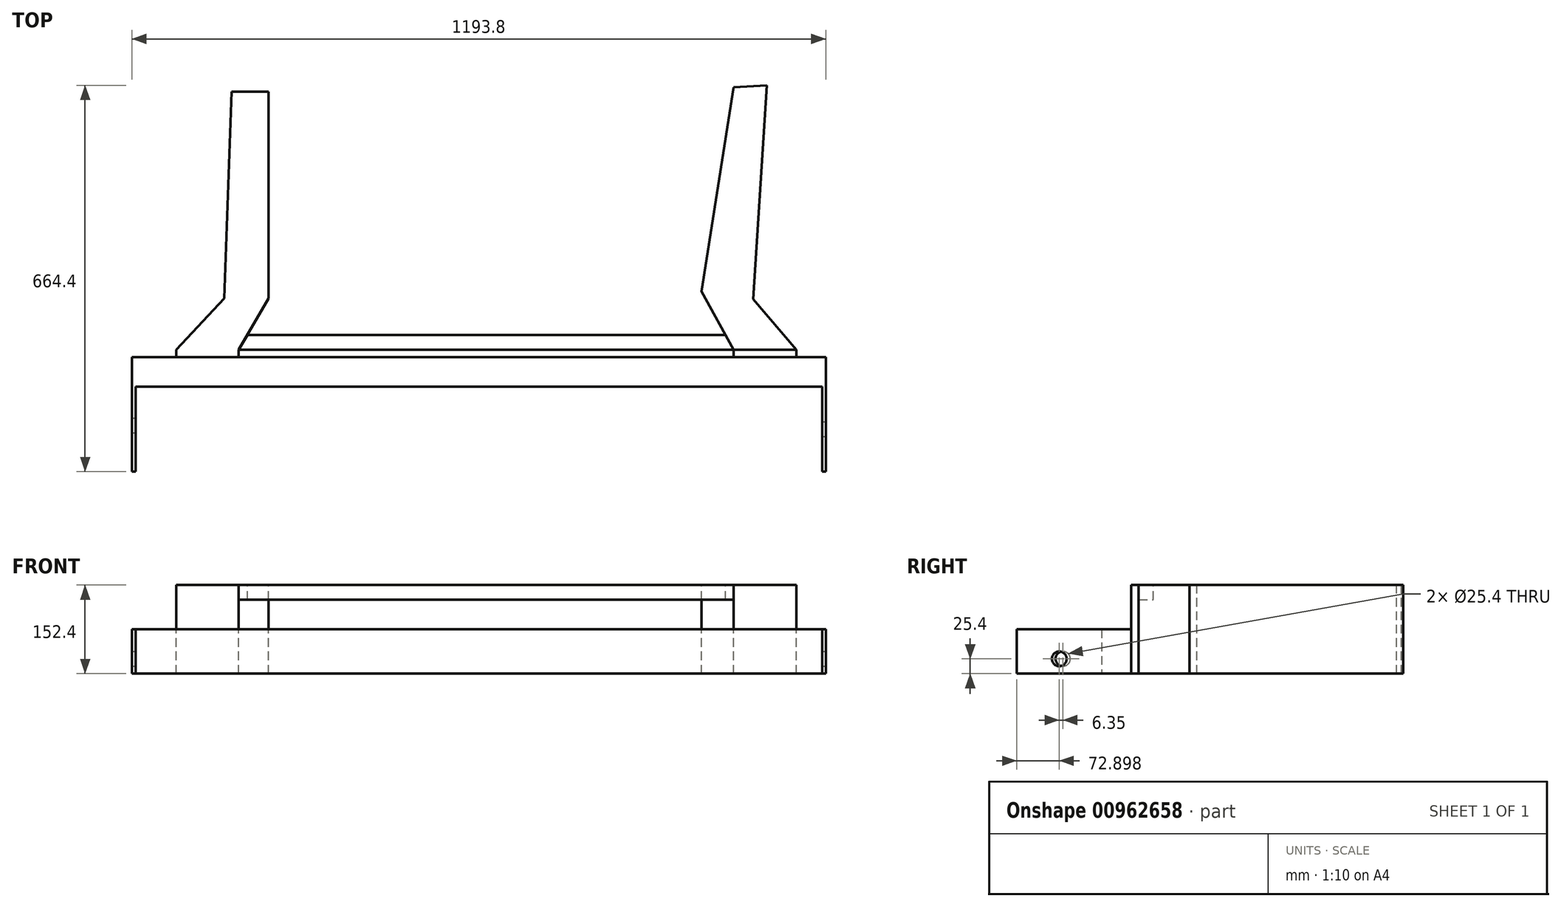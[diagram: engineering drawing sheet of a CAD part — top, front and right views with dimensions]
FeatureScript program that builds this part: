
annotation { "Feature Type Name" : "Feature", "Feature Type Description" : "" }
export const myFeature = defineFeature(function(context is Context, id is Id, definition is map)
    precondition{}
    {
        {
            var Q0;
            Q0=qCreatedBy(makeId("Front.planeOp"),FACE);
            var sketch = newSketch(context, id + "F0", { "sketchPlane" : qUnion([Q0])});
            skLineSegment(sketch, "E0.bottom", {"start": v(-596.9, 38.1) * mm, "end": v(596.9, 38.1) * mm});
            skLineSegment(sketch, "E0.top", {"start": v(-596.9, -38.1) * mm, "end": v(596.9, -38.1) * mm});
            skLineSegment(sketch, "E0.left", {"start": v(-596.9, 38.1) * mm, "end": v(-596.9, -38.1) * mm});
            skLineSegment(sketch, "E0.right", {"start": v(596.9, 38.1) * mm, "end": v(596.9, -38.1) * mm});
            skPoint(sketch, "E0.middle", {"position": v(0, 0) * mm});
            skLineSegment(sketch, "E1", {"start": v(-596.9, 38.1) * mm, "end": v(-590.55, 38.1) * mm});
            skLineSegment(sketch, "E2", {"start": v(-590.55, -38.1) * mm, "end": v(-596.9, -38.1) * mm});
            skLineSegment(sketch, "E3", {"start": v(590.55, -38.1) * mm, "end": v(596.9, -38.1) * mm});
            skLineSegment(sketch, "E4", {"start": v(596.9, 38.1) * mm, "end": v(590.55, 38.1) * mm});
            skSolve(sketch);
        }
        {
            var Q0;
            Q0=qSketchRegion(id+"F0",true);
            var Q1;
            Q1=qSketchRegion(id+"F6",true);
            extrude(context, id + "F1", {"entities" : qUnion([Q0, Q1]), "depth" : 50.8 * mm, "offsetDistance" : 25.4 * mm});
        }
        {
            var Q0;
            Q0=makeQuery(id+"F1.opExtrude","CAP_FACE",FACE,{"disambiguationData":[OSD([sQuery(id+"F0.wireOp",EDGE,"E0.bottom"),sQuery(id+"F0.wireOp",EDGE,"E0.top"),sQuery(id+"F0.wireOp",EDGE,"E0.left"),sQuery(id+"F0.wireOp",EDGE,"E0.right"),sQuery(id+"F0.wireOp",EDGE,"E1"),sQuery(id+"F0.wireOp",EDGE,"E2"),sQuery(id+"F0.wireOp",EDGE,"E3"),sQuery(id+"F0.wireOp",EDGE,"E4")])],"isStart":false});
            var sketch = newSketch(context, id + "F2", { "sketchPlane" : qUnion([Q0])});
            skLineSegment(sketch, "E5", {"start": v(-590.55, 38.1) * mm, "end": v(-590.55, -38.1) * mm});
            skLineSegment(sketch, "E6", {"start": v(-590.55, -38.1) * mm, "end": v(-596.9, -38.1) * mm});
            skLineSegment(sketch, "E7", {"start": v(-596.9, -38.1) * mm, "end": v(-596.9, 38.1) * mm});
            skLineSegment(sketch, "E8", {"start": v(-596.9, 38.1) * mm, "end": v(-590.55, 38.1) * mm});
            skLineSegment(sketch, "E9", {"start": v(590.55, 38.1) * mm, "end": v(590.55, -38.1) * mm});
            skLineSegment(sketch, "E10", {"start": v(590.55, -38.1) * mm, "end": v(596.9, -38.1) * mm});
            skLineSegment(sketch, "E11", {"start": v(596.9, -38.1) * mm, "end": v(596.9, 38.1) * mm});
            skLineSegment(sketch, "E12", {"start": v(596.9, 38.1) * mm, "end": v(590.55, 38.1) * mm});
            skSolve(sketch);
        }
        {
            var Q0;
            Q0=makeQuery(id+"F2.imprint","IMPRINT",FACE,{"disambiguationData":[TD([[makeQuery(id+"F2.imprint","IMPRINT",EDGE,{"derivedFrom":sQuery(id+"F2.wireOp",EDGE,"E5")}),-1.0]])]});
            var Q1;
            Q1=makeQuery(id+"F2.imprint","IMPRINT",FACE,{"disambiguationData":[TD([[makeQuery(id+"F2.imprint","IMPRINT",EDGE,{"derivedFrom":sQuery(id+"F2.wireOp",EDGE,"E9")}),1.0]])]});
            extrude(context, id + "F3", {"entities" : qUnion([Q0, Q1]), "operationType" : NewBodyOperationType.ADD, "depth" : 146.05 * mm, "offsetDistance" : 25.4 * mm});
        }
        {
            var Q0;
            Q0=makeQuery(id+"F3.opExtrude","SWEPT_FACE",FACE,{"disambiguationData":[OSD([sQuery(id+"F2.wireOp",EDGE,"E5")])]});
            var sketch = newSketch(context, id + "F4", { "sketchPlane" : qUnion([Q0])});
            skCircle(sketch, "E13", {"center": v(-117.6, -12.7) * mm, "radius": 12.7 * mm});
            skSolve(sketch);
        }
        {
            var Q0;
            Q0=qSketchRegion(id+"F4",true);
            extrude(context, id + "F5", {"entities" : qUnion([Q0]), "operationType" : NewBodyOperationType.REMOVE, "oppositeDirection" : true, "depth" : 25.4 * mm, "offsetDistance" : 25.4 * mm});
        }
        {
            var Q0;
            Q0=makeQuery(id+"F3.boolean.opBoolean","MERGE",FACE,{"derivedFrom":[makeQuery(id+"F1.opExtrude","SWEPT_FACE",FACE,{"disambiguationData":[OSD([sQuery(id+"F0.wireOp",EDGE,"E0.right")])]}),makeQuery(id+"F3.opExtrude","SWEPT_FACE",FACE,{"disambiguationData":[OSD([sQuery(id+"F2.wireOp",EDGE,"E11")])]})]});
            var sketch = newSketch(context, id + "F6", { "sketchPlane" : qUnion([Q0])});
            skCircle(sketch, "E14", {"center": v(-123.95, -12.7) * mm, "radius": 12.7 * mm});
            skSolve(sketch);
        }
        {
            var Q0;
            Q0=qSketchRegion(id+"F6",true);
            extrude(context, id + "F7", {"entities" : qUnion([Q0]), "operationType" : NewBodyOperationType.REMOVE, "oppositeDirection" : true, "depth" : 25.4 * mm, "offsetDistance" : 25.4 * mm});
        }
        {
            var Q0;
            Q0=makeQuery(id+"F1.opExtrude","CAP_FACE",FACE,{"disambiguationData":[OSD([sQuery(id+"F0.wireOp",EDGE,"E0.bottom"),sQuery(id+"F0.wireOp",EDGE,"E0.top"),sQuery(id+"F0.wireOp",EDGE,"E0.left"),sQuery(id+"F0.wireOp",EDGE,"E0.right"),sQuery(id+"F0.wireOp",EDGE,"E1"),sQuery(id+"F0.wireOp",EDGE,"E2"),sQuery(id+"F0.wireOp",EDGE,"E3"),sQuery(id+"F0.wireOp",EDGE,"E4")])],"isStart":true});
            var sketch = newSketch(context, id + "F8", { "sketchPlane" : qUnion([Q0])});
            skLineSegment(sketch, "E15.bottom", {"start": v(-546.1, -38.1) * mm, "end": v(-438.15, -38.1) * mm});
            skLineSegment(sketch, "E15.top", {"start": v(-546.1, 114.3) * mm, "end": v(-438.15, 114.3) * mm});
            skLineSegment(sketch, "E15.left", {"start": v(-546.1, -38.1) * mm, "end": v(-546.1, 114.3) * mm});
            skLineSegment(sketch, "E15.right", {"start": v(-438.15, -38.1) * mm, "end": v(-438.15, 114.3) * mm});
            skLineSegment(sketch, "E16.bottom", {"start": v(412.75, -38.1) * mm, "end": v(520.7, -38.1) * mm});
            skLineSegment(sketch, "E16.top", {"start": v(412.75, 114.3) * mm, "end": v(520.7, 114.3) * mm});
            skLineSegment(sketch, "E16.left", {"start": v(412.75, -38.1) * mm, "end": v(412.75, 114.3) * mm});
            skLineSegment(sketch, "E16.right", {"start": v(520.7, -38.1) * mm, "end": v(520.7, 114.3) * mm});
            skSolve(sketch);
        }
        {
            var Q0;
            Q0=qSketchRegion(id+"F8",true);
            extrude(context, id + "F9", {"entities" : qUnion([Q0]), "operationType" : NewBodyOperationType.ADD, "depth" : 12.7 * mm, "offsetDistance" : 25.4 * mm});
        }
        {
            var Q0;
            Q0=makeQuery(id+"F9.opExtrude","SWEPT_FACE",FACE,{"disambiguationData":[OSD([sQuery(id+"F8.wireOp",EDGE,"E15.top")])]});
            var sketch = newSketch(context, id + "F10", { "sketchPlane" : qUnion([Q0])});
            skLineSegment(sketch, "E17", {"start": v(438.15, 12.7) * mm, "end": v(383.38, 113.02) * mm});
            skLineSegment(sketch, "E18", {"start": v(383.38, 113.02) * mm, "end": v(438.15, 464.38) * mm});
            skLineSegment(sketch, "E19", {"start": v(546.1, 12.7) * mm, "end": v(472.28, 99.97) * mm});
            skLineSegment(sketch, "E20", {"start": v(472.28, 99.97) * mm, "end": v(495.3, 467.55) * mm});
            skLineSegment(sketch, "E21", {"start": v(438.15, 464.38) * mm, "end": v(495.3, 467.55) * mm});
            skSolve(sketch);
        }
        {
            var Q0;
            Q0=makeQuery(id+"F9.opExtrude","SWEPT_FACE",FACE,{"disambiguationData":[OSD([sQuery(id+"F8.wireOp",EDGE,"E16.top")])]});
            var sketch = newSketch(context, id + "F11", { "sketchPlane" : qUnion([Q0])});
            skLineSegment(sketch, "E22", {"start": v(-412.75, 12.7) * mm, "end": v(-361.95, 100.69) * mm});
            skLineSegment(sketch, "E23", {"start": v(-361.95, 100.69) * mm, "end": v(-361.95, 456.29) * mm});
            skLineSegment(sketch, "E24", {"start": v(-361.95, 456.29) * mm, "end": v(-425.45, 456.29) * mm});
            skLineSegment(sketch, "E25", {"start": v(-425.45, 456.29) * mm, "end": v(-438.15, 100.69) * mm});
            skLineSegment(sketch, "E26", {"start": v(-438.15, 100.69) * mm, "end": v(-520.7, 12.7) * mm});
            skSolve(sketch);
        }
        {
            var Q0;
            Q0=makeQuery(id+"F11.imprint","IMPRINT",FACE,{"disambiguationData":[TD([[makeQuery(id+"F11.imprint","IMPRINT",EDGE,{"derivedFrom":sQuery(id+"F11.wireOp",EDGE,"E22")}),1.0]])]});
            extrude(context, id + "F12", {"entities" : qUnion([Q0]), "operationType" : NewBodyOperationType.ADD, "oppositeDirection" : true, "depth" : 152.4 * mm, "offsetDistance" : 25.4 * mm});
        }
        {
            var Q0;
            {var subQ0=sQuery(id+"F8.wireOp",EDGE,"E16.top");Q0=makeQuery(id+"F12.boolean.opBoolean","MERGE",FACE,{"derivedFrom":[makeQuery(id+"F9.opExtrude","SWEPT_FACE",FACE,{"disambiguationData":[OSD([subQ0])]}),makeQuery(id+"F12.opExtrude","CAP_FACE",FACE,{"disambiguationData":[OSD([subQ0,sQuery(id+"F11.wireOp",EDGE,"E22"),sQuery(id+"F11.wireOp",EDGE,"E23"),sQuery(id+"F11.wireOp",EDGE,"E24"),sQuery(id+"F11.wireOp",EDGE,"E25"),sQuery(id+"F11.wireOp",EDGE,"E26")])],"isStart":true})]});}
            var sketch = newSketch(context, id + "F13", { "sketchPlane" : qUnion([Q0])});
            skLineSegment(sketch, "E27.bottom", {"start": v(-450.85, 0) * mm, "end": v(438.15, 0) * mm});
            skLineSegment(sketch, "E28", {"start": v(-412.75, 12.7) * mm, "end": v(438.15, 12.7) * mm});
            skLineSegment(sketch, "E29", {"start": v(438.15, 12.7) * mm, "end": v(424.28, 38.1) * mm});
            skLineSegment(sketch, "E30", {"start": v(424.28, 38.1) * mm, "end": v(-398.09, 38.1) * mm});
            skLineSegment(sketch, "E31", {"start": v(-398.09, 38.1) * mm, "end": v(-412.75, 12.7) * mm});
            skSolve(sketch);
        }
        {
            var Q0;
            Q0=makeQuery(id+"F13.imprint","IMPRINT",FACE,{"disambiguationData":[TD([[makeQuery(id+"F13.imprint","IMPRINT",EDGE,{"derivedFrom":sQuery(id+"F13.wireOp",EDGE,"E28")}),1.0]])]});
            extrude(context, id + "F14", {"entities" : qUnion([Q0]), "oppositeDirection" : true, "depth" : 25.4 * mm, "offsetDistance" : 25.4 * mm});
        }
        {
            var Q0;
            Q0=makeQuery(id+"F10.imprint","IMPRINT",FACE,{"disambiguationData":[TD([[makeQuery(id+"F10.imprint","IMPRINT",EDGE,{"derivedFrom":sQuery(id+"F10.wireOp",EDGE,"E17")}),-1.0]])]});
            extrude(context, id + "F15", {"entities" : qUnion([Q0]), "oppositeDirection" : true, "depth" : 152.4 * mm, "offsetDistance" : 25.4 * mm});
        }
    });
